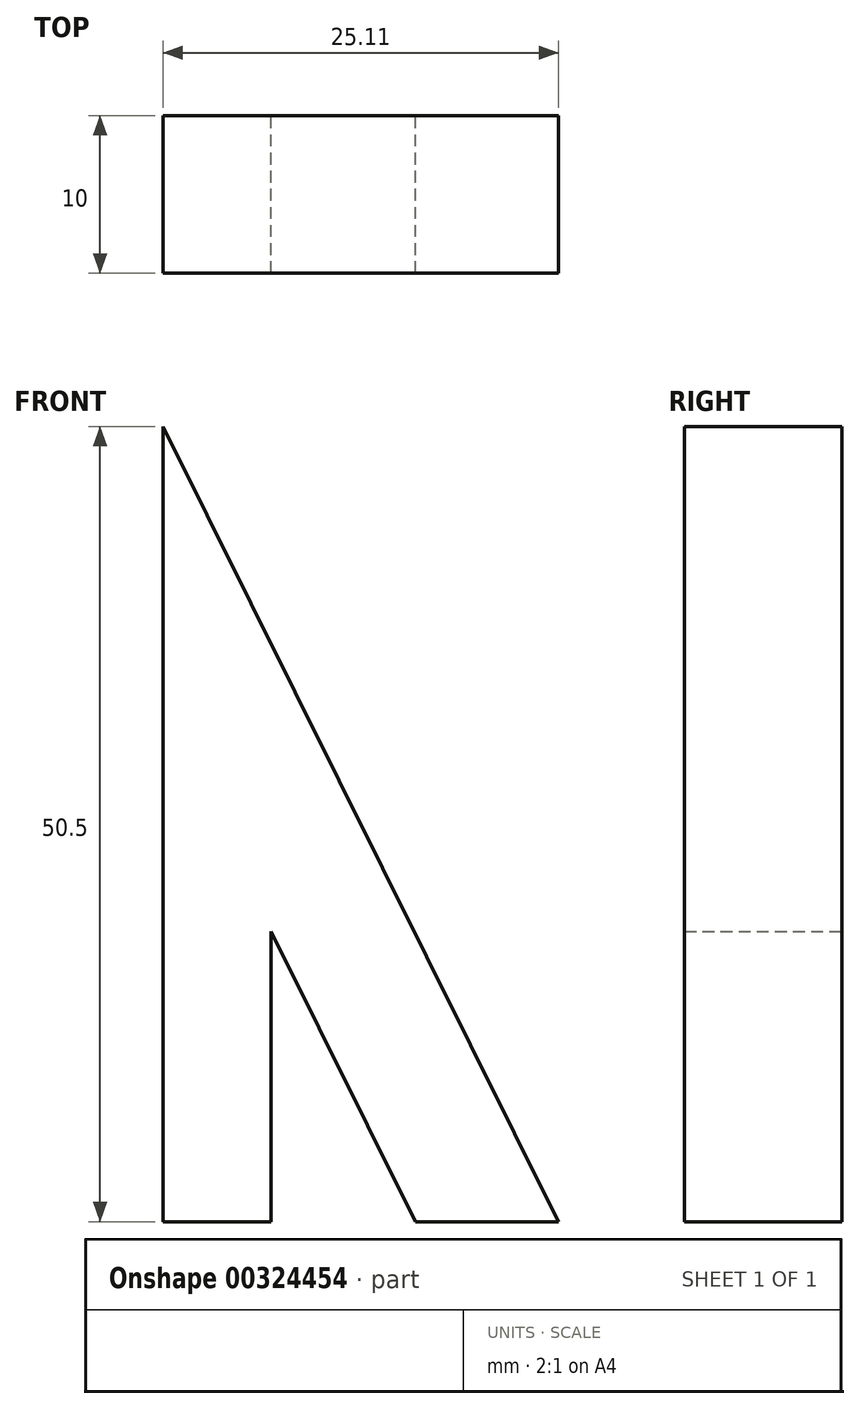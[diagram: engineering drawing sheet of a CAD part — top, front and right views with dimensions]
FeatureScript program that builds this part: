
annotation { "Feature Type Name" : "Feature", "Feature Type Description" : "" }
export const myFeature = defineFeature(function(context is Context, id is Id, definition is map)
    precondition{}
    {
        {
            var Q0;
            Q0=qCreatedBy(makeId("Front.planeOp"),FACE);
            var sketch = newSketch(context, id + "F0", { "sketchPlane" : qUnion([Q0])});
            skLineSegment(sketch, "E0", {"start": v(0, 0) * mm, "end": v(0, 50.5) * mm});
            skLineSegment(sketch, "E1", {"start": v(0, 50.5) * mm, "end": v(25.11, 0) * mm});
            skLineSegment(sketch, "E2", {"start": v(25.11, 0) * mm, "end": v(16.01, 0) * mm});
            skLineSegment(sketch, "E3", {"start": v(16.01, 0) * mm, "end": v(6.84, 18.45) * mm});
            skLineSegment(sketch, "E4", {"start": v(6.84, 18.45) * mm, "end": v(6.84, 0) * mm});
            skLineSegment(sketch, "E5", {"start": v(6.84, 0) * mm, "end": v(0, 0) * mm});
            skSolve(sketch);
        }
        {
            var Q0;
            Q0=makeQuery(id+"F0.imprint","IMPRINT",FACE,{"disambiguationData":[TD([[makeQuery(id+"F0.imprint","IMPRINT",EDGE,{"derivedFrom":sQuery(id+"F0.wireOp",EDGE,"E0")}),-1.0]])]});
            extrude(context, id + "F1", {"entities" : qUnion([Q0]), "depth" : 10 * mm});
        }
    });
